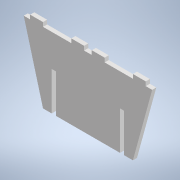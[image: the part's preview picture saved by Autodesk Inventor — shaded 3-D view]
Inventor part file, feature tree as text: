
AUTODESK INVENTOR PART (.ipt)
format: ipt  version: 2022 (Build 260153000, 153)  size: 131,584 bytes
history: native  units: mm
features: reference x5, other x4, extrude x1, sketch x1
ambient origin geometry x8: Origin, YZ Plane, XZ Plane, XY Plane, X Axis, Y Axis, Z Axis, Center Point
bodies: Solid1 (feature_tree)
feature tree (11):
  extrude  "Extrusion1"  Depth=10.0mm
  sketch  "Sketch1"  dims[d0=55.0mm d1=35.0mm d2=50.0mm d3=25.0mm d4=30.0mm d5=3.2mm d6=3.2mm d7=10.0mm d8=3.0mm d9=3.2mm d10=0.0mm d11=3.2mm d12=10.0mm d13=5.0mm]
  reference  "Reference1"
  reference  "Reference2"
  reference  "Reference3"
  reference  "Reference4"
  reference  "Reference5"
  other  "<userpath>\OneDrive\Escritorio\Mini_Proyecto_Diseno\Diseno_18012\Modelo_MPD\Carril.iam"
  other  "Carril.iam"
  other  "Base:1"
  other  "Base:2"
